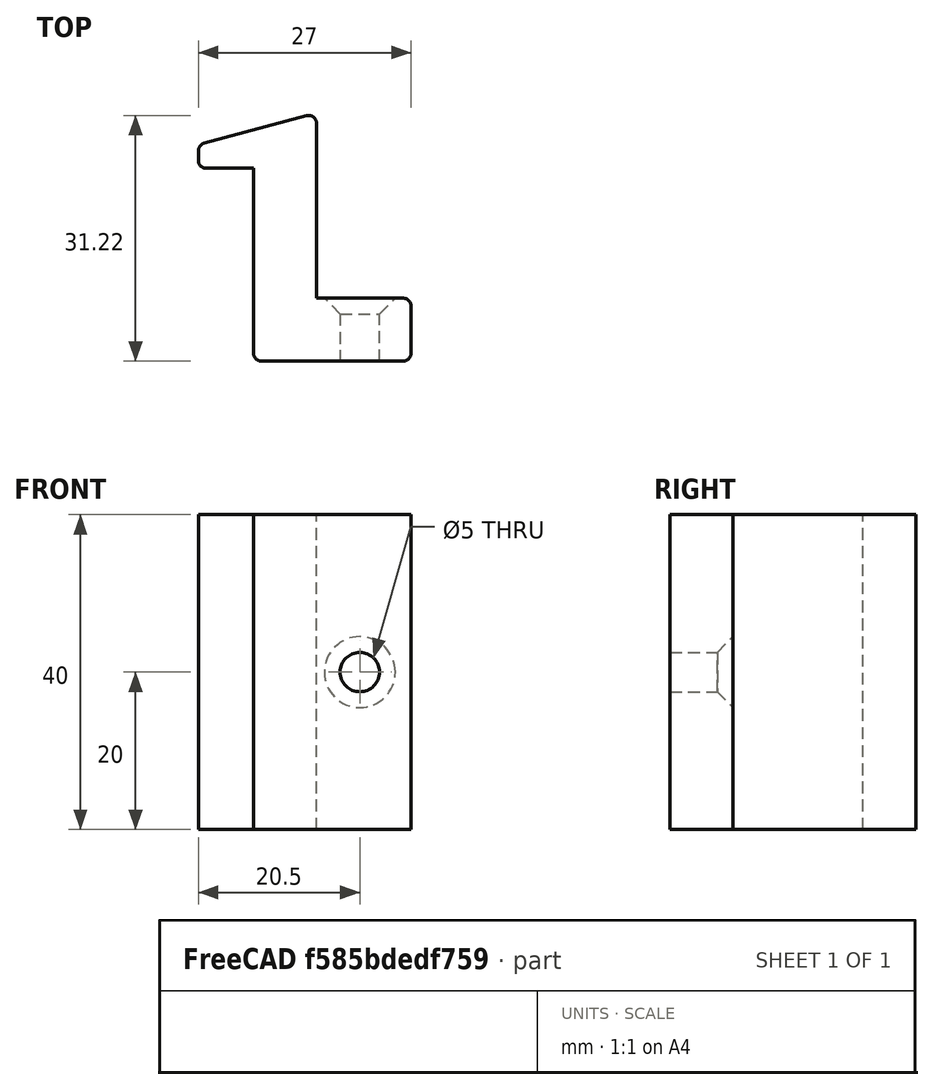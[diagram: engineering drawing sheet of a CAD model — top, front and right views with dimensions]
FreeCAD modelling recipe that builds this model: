
FCSTD DOCUMENT  (FreeCAD 0.19R)
Label: 18650AAChargerClip
License: All rights reserved
LicenseURL: http://en.wikipedia.org/wiki/All_rights_reserved
objects: Sketcher::SketchObject×2, PartDesign::Pad×1, PartDesign::Pocket×1, PartDesign::Chamfer×1, PartDesign::Fillet×1, PartDesign::Body×1, Mesh::Feature×1
note: 11 computed .brp shape members not serialized (recipe doc carries the construction recipe); baked Part::Feature solids carry a one-line shape summary decoded from their .brp

FEATURE [Sketcher::SketchObject] Sketch
  FullyConstrained = true
  MapMode = 5
  Support = -> [XY_Plane]
  sketch-geometry (8):
    g0: LineSegment StartX=0 StartY=-8 StartZ=0 EndX=0 EndY=16.5 EndZ=0
    g1: LineSegment StartX=0 StartY=16.5 StartZ=0 EndX=-7 EndY=16.5 EndZ=0
    g2: LineSegment StartX=-7 StartY=16.5 StartZ=0 EndX=-7 EndY=19.5 EndZ=0
    g3: LineSegment StartX=-7 StartY=19.5 StartZ=0 EndX=8 EndY=23.5192 EndZ=0
    g4: LineSegment StartX=8 StartY=23.5192 StartZ=0 EndX=8 EndY=0 EndZ=0
    g5: LineSegment StartX=8 StartY=0 StartZ=0 EndX=20 EndY=0 EndZ=0
    g6: LineSegment StartX=20 StartY=0 StartZ=0 EndX=20 EndY=-8 EndZ=0
    g7: LineSegment StartX=20 StartY=-8 StartZ=0 EndX=0 EndY=-8 EndZ=0
  constraints (24):
    c: PointOnObject(g0,g-2)
    c: PointOnObject(g0,g-2)
    c: Coincident(g0,g1)
    c: Coincident(g1,g2)
    c: Vertical(g2)
    c: Coincident(g2,g3)
    c: Coincident(g3,g4)
    c: PointOnObject(g4,g-1)
    c: Vertical(g4)
    c: Coincident(g4,g5)
    c: PointOnObject(g5,g-1)
    c: Coincident(g5,g6)
    c: Coincident(g6,g7)
    c: Coincident(g7,g0)
    c: Horizontal(g7)
    c: Vertical(g6)
    c: Horizontal(g1)
    c: Distance(g1) = 7
    c: Distance(g2) = 3
    c: Distance(g4,g0) = 8
    c: Distance(g6) = 8
    c: Distance(g7) = 20
    c: Distance(g0) = 24.5
    c: Angle(g3) = 0.261799
FEATURE [PartDesign::Pad] Pad
  Direction = (1,1,1)
  Length = 40
  Length2 = 100
  Profile = -> Sketch
  Type = 0
FEATURE [Sketcher::SketchObject] Sketch001
  FullyConstrained = true
  MapMode = 5
  Placement = pos=(0,0,0) rot=(0,0.707107,0.707107;3.14159rad)
  Support = -> [Pad]
  sketch-geometry (1):
    g0: Circle CenterX=-13.5 CenterY=20 CenterZ=0 NormalX=0 NormalY=0 NormalZ=1 AngleXU=0 Radius=2.5
  constraints (3):
    c: Diameter(g0) = 5
    c: DistanceX(g0) = -13.5
    c: DistanceY(g0) = 20
FEATURE [PartDesign::Pocket] Pocket
  BaseFeature = -> Pad
  Length = 5
  Length2 = 100
  Profile = -> Sketch001
  Type = 1
FEATURE [PartDesign::Chamfer] Chamfer
  Angle = 45
  Base = -> Pocket [Edge23]
  BaseFeature = -> Pocket
  ChamferType = 0
  FlipDirection = false
  Size = 2
  Size2 = 1
  SupportTransform = false
FEATURE [PartDesign::Fillet] Fillet
  Base = -> Chamfer [Edge27,Edge13,Edge6,Edge9,Edge28,Edge29]
  BaseFeature = -> Chamfer
  Radius = 1
  SupportTransform = false
FEATURE [PartDesign::Body] Body
  Group = -> [Sketch,Pad,Sketch001,Pocket,Chamfer,Fillet]
  Origin = -> Origin
  Tip = -> Fillet
FEATURE [Mesh::Feature] Mesh  label="Fillet (Meshed)"
